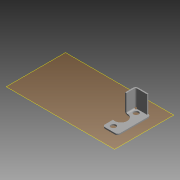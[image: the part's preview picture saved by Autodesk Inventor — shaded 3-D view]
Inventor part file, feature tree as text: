
AUTODESK INVENTOR PART (.ipt)
format: ipt  version: 2015 (Build 190159000, 159)  size: 176,128 bytes
history: native  units: mm
features: sheet_metal_op x10, sketch x4, other x4, reference x3, plane x1, hole x1
ambient origin geometry x8: Origin, YZ Plane, XZ Plane, XY Plane, X Axis, Y Axis, Z Axis, Center Point
bodies: Solid1 (feature_tree)
feature tree (23):
  plane  "Work Plane1"
  sheet_metal_op  "Face1"
  sheet_metal_op  "Flange4"
  sheet_metal_op  "Flange5"
  sheet_metal_op  "Flange6"
  hole  "Hole3"  [1 undecoded]
  sketch  "Sketch1"  dims[d0=5.0mm d2=1.0mm]
  reference  "Reference1"
  reference  "Reference2"
  reference  "Reference3"
  other  "Plate1"
  sketch  "Sketch5"  dims[d53=2.0mm]
  other  "Plate5"
  sheet_metal_op  "Bend4"
  sheet_metal_op  "Corner4"
  sketch  "Sketch6"  dims[d57=8.0mm]
  other  "Plate6"
  sheet_metal_op  "Bend5"
  sheet_metal_op  "Corner5"
  sketch  "Sketch7"  dims[d60=1.0mm d61=0.5mm d62=2.0mm d63=1.0mm d64=15.0mm d65=90.0deg d66=1.0mm d67=4.0mm d68=1.0mm d69=1.0mm d70=1.0mm d71=0.5mm d72=2.0mm d73=1.0mm d74=12.0mm d75=90.0deg d76=1.0mm d77=4.0mm d78=1.0mm d79=1.0mm d80=1.0mm d81=0.5mm d82=2.0mm d83=1.0mm d84=1.0mm d85=0.0mm d86=1.0mm d87=4.0mm d88=1.0mm d89=1.0mm d90=4.0mm d91=4.0mm d92=3.0mm d93=6.0mm d94=4.0mm d95=2.0mm d96=90.0deg d97=1.0mm d98=20.594885mm d99=4.0mm d100=135.0deg]
  other  "Plate7"
  sheet_metal_op  "Bend6"
  sheet_metal_op  "Corner6"
note: 1 required parameter value undecoded (feature->parameter linkage not recoverable at this tier; creation-order binding heuristic only, values carry confidence <= 0.55)
